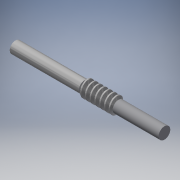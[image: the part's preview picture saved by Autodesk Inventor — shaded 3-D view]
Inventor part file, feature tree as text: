
AUTODESK INVENTOR PART (.ipt)
format: ipt  version: 2018 (Build 220112000, 112)  size: 437,760 bytes
history: native  units: in
note: dims shown in document units (in); Inventor stores cm internally (conversion verified against a paired STEP export)
features: other x3, extrude x3, sketch x3
ambient origin geometry x8: Origin, YZ Plane, XZ Plane, XY Plane, X Axis, Y Axis, Z Axis, Center Point
bodies: Solid1 (feature_tree)
feature tree (9):
  other  "Worm"
  extrude  "Extrusion1"  Depth=0.25in
  extrude  "Extrusion2"  Depth=1.9685in
  extrude  "Extrusion3"  Depth=0.5in
  other  "Solid1::Worm"
  other  "TaggingFeature1"
  sketch  "Sketch1"  dims[d0=0.25in d1=0.5in]
  sketch  "Sketch2"  dims[d2=1.9685in d3=0.0in d4=0.5in]
  sketch  "Sketch3"  dims[d5=1.5748in d6=0.0in d7=0.5in d8=0.9843in d9=0.0in]
